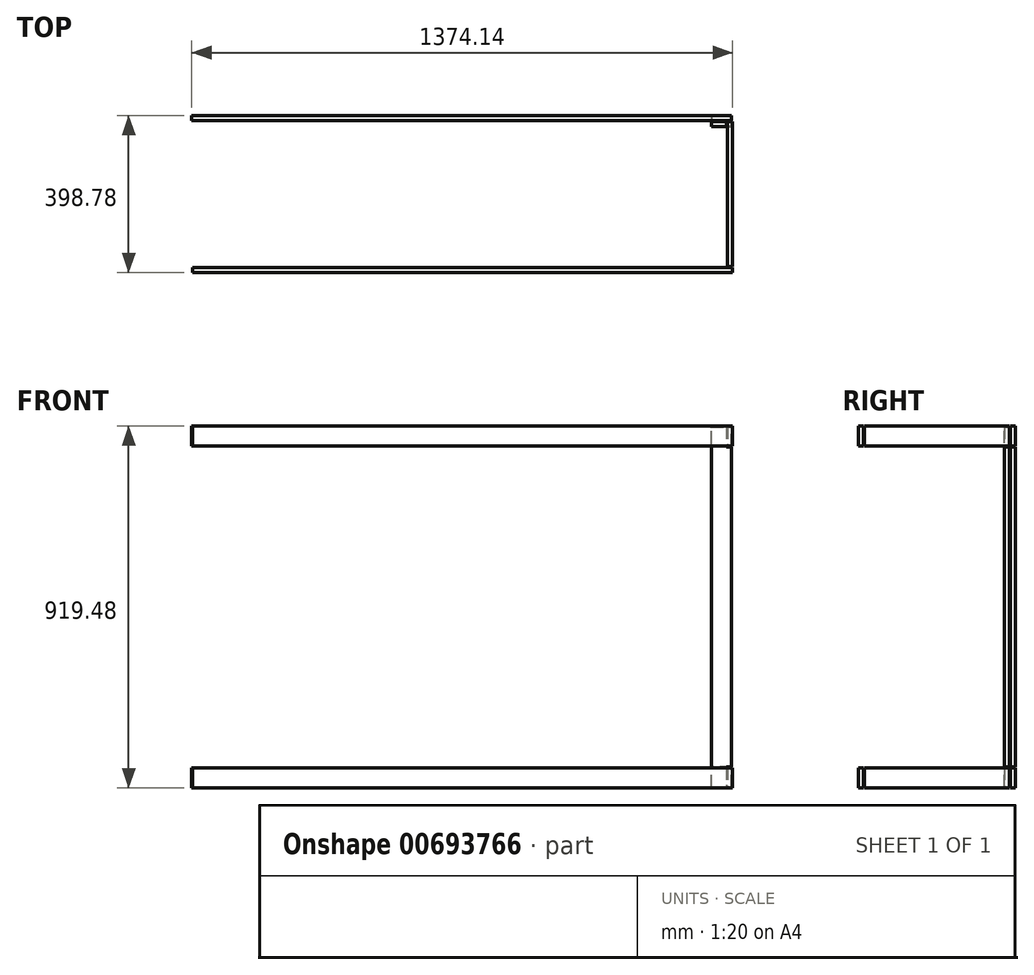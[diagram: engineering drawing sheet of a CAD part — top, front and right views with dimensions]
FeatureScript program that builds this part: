
annotation { "Feature Type Name" : "Feature", "Feature Type Description" : "" }
export const myFeature = defineFeature(function(context is Context, id is Id, definition is map)
    precondition{}
    {
        {
            var Q0;
            Q0=qCreatedBy(makeId("Front.planeOp"),FACE);
            var sketch = newSketch(context, id + "F0", { "sketchPlane" : qUnion([Q0])});
            skLineSegment(sketch, "E0.bottom", {"start": v(0, 0) * mm, "end": v(50.8, 0) * mm});
            skLineSegment(sketch, "E0.top", {"start": v(0, 914.4) * mm, "end": v(50.8, 914.4) * mm});
            skLineSegment(sketch, "E0.left", {"start": v(0, 0) * mm, "end": v(0, 914.4) * mm});
            skLineSegment(sketch, "E0.right", {"start": v(50.8, 0) * mm, "end": v(50.8, 914.4) * mm});
            skSolve(sketch);
        }
        {
            var Q0;
            Q0 = qSketchRegion(id + "F0", true);
            extrude(context, id + "F1", {"entities" : qUnion([Q0]), "depth" : 12.7 * mm, "offsetDistance" : 25.4 * mm});
        }
        {
            var Q0;
            Q0=makeQuery(id+"F1.opExtrude","CAP_FACE",FACE,{"disambiguationData":[OSD([sQuery(id+"F0.wireOp",EDGE,"E0.bottom"),sQuery(id+"F0.wireOp",EDGE,"E0.top"),sQuery(id+"F0.wireOp",EDGE,"E0.left"),sQuery(id+"F0.wireOp",EDGE,"E0.right")])],"isStart":true});
            cPlane(context, id + "F2", {"entities" : qUnion([Q0]), "cplaneType" : CPlaneType.OFFSET, "offset" : 2.54 * mm, "width" : 152.4 * mm, "height" : 152.4 * mm});
        }
        {
            var Q0;
            Q0=qCreatedBy(id+"F2.planeOp",FACE);
            var sketch = newSketch(context, id + "F3", { "sketchPlane" : qUnion([Q0])});
            skLineSegment(sketch, "E1.bottom", {"start": v(-50.8, 863.6) * mm, "end": v(0, 863.6) * mm});
            skLineSegment(sketch, "E1.top", {"start": v(-50.8, 50.8) * mm, "end": v(0, 50.8) * mm});
            skLineSegment(sketch, "E1.left", {"start": v(-50.8, 863.6) * mm, "end": v(-50.8, 50.8) * mm});
            skLineSegment(sketch, "E1.right", {"start": v(0, 863.6) * mm, "end": v(0, 50.8) * mm});
            skSolve(sketch);
        }
        {
            var Q0;
            Q0 = qSketchRegion(id + "F3", true);
            extrude(context, id + "F4", {"entities" : qUnion([Q0]), "depth" : 12.7 * mm, "offsetDistance" : 25.4 * mm});
        }
        {
            var Q0;
            Q0=makeQuery(id+"F4.opExtrude","SWEPT_FACE",FACE,{"disambiguationData":[OSD([sQuery(id+"F3.wireOp",EDGE,"E1.top")])]});
            cPlane(context, id + "F5", {"entities" : qUnion([Q0]), "cplaneType" : CPlaneType.OFFSET, "offset" : 2.54 * mm, "width" : 152.4 * mm, "height" : 152.4 * mm});
        }
        {
            var Q0;
            Q0=qCreatedBy(id+"F5.planeOp",FACE);
            var sketch = newSketch(context, id + "F6", { "sketchPlane" : qUnion([Q0])});
            skLineSegment(sketch, "E2.bottom", {"start": v(50.8, -2.54) * mm, "end": v(-1320.8, -2.54) * mm});
            skLineSegment(sketch, "E2.top", {"start": v(50.8, -15.24) * mm, "end": v(-1320.8, -15.24) * mm});
            skLineSegment(sketch, "E2.left", {"start": v(50.8, -2.54) * mm, "end": v(50.8, -15.24) * mm});
            skLineSegment(sketch, "E2.right", {"start": v(-1320.8, -2.54) * mm, "end": v(-1320.8, -15.24) * mm});
            skSolve(sketch);
        }
        {
            var Q0;
            Q0=makeQuery(id+"F6.imprint","IMPRINT",FACE,{"disambiguationData":[TD([[makeQuery(id+"F6.imprint","IMPRINT",EDGE,{"derivedFrom":sQuery(id+"F6.wireOp",EDGE,"E2.bottom")}),1.0]])]});
            extrude(context, id + "F7", {"entities" : qUnion([Q0]), "depth" : 50.8 * mm, "offsetDistance" : 25.4 * mm});
        }
        {
            var Q0;
            Q0=makeQuery(id+"F4.opExtrude","SWEPT_FACE",FACE,{"disambiguationData":[OSD([sQuery(id+"F3.wireOp",EDGE,"E1.bottom")])]});
            cPlane(context, id + "F8", {"entities" : qUnion([Q0]), "cplaneType" : CPlaneType.OFFSET, "offset" : 2.54 * mm, "width" : 152.4 * mm, "height" : 152.4 * mm});
        }
        {
            var Q0;
            Q0=qCreatedBy(id+"F8.planeOp",FACE);
            var sketch = newSketch(context, id + "F9", { "sketchPlane" : qUnion([Q0])});
            skLineSegment(sketch, "E3.bottom", {"start": v(50.8, 15.24) * mm, "end": v(-1320.8, 15.24) * mm});
            skLineSegment(sketch, "E3.top", {"start": v(50.8, 2.54) * mm, "end": v(-1320.8, 2.54) * mm});
            skLineSegment(sketch, "E3.left", {"start": v(50.8, 15.24) * mm, "end": v(50.8, 2.54) * mm});
            skLineSegment(sketch, "E3.right", {"start": v(-1320.8, 15.24) * mm, "end": v(-1320.8, 2.54) * mm});
            skSolve(sketch);
        }
        {
            var Q0;
            Q0=makeQuery(id+"F9.imprint","IMPRINT",FACE,{"disambiguationData":[TD([[makeQuery(id+"F9.imprint","IMPRINT",EDGE,{"derivedFrom":sQuery(id+"F9.wireOp",EDGE,"E3.bottom")}),1.0]])]});
            extrude(context, id + "F10", {"entities" : qUnion([Q0]), "depth" : 50.8 * mm, "offsetDistance" : 25.4 * mm});
        }
        {
            var Q0;
            Q0=makeQuery(id+"F1.opExtrude","CAP_FACE",FACE,{"disambiguationData":[OSD([sQuery(id+"F0.wireOp",EDGE,"E0.bottom"),sQuery(id+"F0.wireOp",EDGE,"E0.top"),sQuery(id+"F0.wireOp",EDGE,"E0.left"),sQuery(id+"F0.wireOp",EDGE,"E0.right")])],"isStart":false});
            var sketch = newSketch(context, id + "F11", { "sketchPlane" : qUnion([Q0])});
            skLineSegment(sketch, "E4.bottom", {"start": v(38.1, 914.4) * mm, "end": v(50.8, 914.4) * mm});
            skLineSegment(sketch, "E4.top", {"start": v(38.1, 863.6) * mm, "end": v(50.8, 863.6) * mm});
            skLineSegment(sketch, "E4.left", {"start": v(38.1, 914.4) * mm, "end": v(38.1, 863.6) * mm});
            skLineSegment(sketch, "E4.right", {"start": v(50.8, 914.4) * mm, "end": v(50.8, 863.6) * mm});
            skSolve(sketch);
        }
        {
            var Q0;
            Q0 = qSketchRegion(id + "F11", true);
            extrude(context, id + "F12", {"entities" : qUnion([Q0]), "operationType" : NewBodyOperationType.REMOVE, "oppositeDirection" : true, "depth" : 12.7 * mm, "offsetDistance" : 25.4 * mm});
        }
        {
            var Q0;
            Q0=makeQuery(id+"F12.boolean.opBoolean","COPY",FACE,{"derivedFrom":makeQuery(id+"F12.opExtrude","SWEPT_FACE",FACE,{"disambiguationData":[OSD([sQuery(id+"F11.wireOp",EDGE,"E4.left")])]})});
            cPlane(context, id + "F13", {"entities" : qUnion([Q0]), "cplaneType" : CPlaneType.OFFSET, "offset" : 2.54 * mm, "width" : 152.4 * mm, "height" : 152.4 * mm});
        }
        {
            var Q0;
            Q0=qCreatedBy(id+"F13.planeOp",FACE);
            var sketch = newSketch(context, id + "F14", { "sketchPlane" : qUnion([Q0])});
            skLineSegment(sketch, "E5.bottom", {"start": v(-368.3, 916.94) * mm, "end": v(0, 916.94) * mm});
            skLineSegment(sketch, "E5.top", {"start": v(-368.3, 866.14) * mm, "end": v(0, 866.14) * mm});
            skLineSegment(sketch, "E5.left", {"start": v(-368.3, 916.94) * mm, "end": v(-368.3, 866.14) * mm});
            skLineSegment(sketch, "E5.right", {"start": v(0, 916.94) * mm, "end": v(0, 866.14) * mm});
            skSolve(sketch);
        }
        {
            var Q0;
            Q0=makeQuery(id+"F14.imprint","IMPRINT",FACE,{"disambiguationData":[TD([[makeQuery(id+"F14.imprint","IMPRINT",EDGE,{"derivedFrom":sQuery(id+"F14.wireOp",EDGE,"E5.bottom")}),-1.0]])]});
            extrude(context, id + "F15", {"entities" : qUnion([Q0]), "depth" : 12.7 * mm, "offsetDistance" : 25.4 * mm});
        }
        {
            var Q0;
            Q0=makeQuery(id+"F1.opExtrude","CAP_FACE",FACE,{"disambiguationData":[OSD([sQuery(id+"F0.wireOp",EDGE,"E0.bottom"),sQuery(id+"F0.wireOp",EDGE,"E0.top"),sQuery(id+"F0.wireOp",EDGE,"E0.left"),sQuery(id+"F0.wireOp",EDGE,"E0.right")])],"isStart":false});
            var sketch = newSketch(context, id + "F16", { "sketchPlane" : qUnion([Q0])});
            skLineSegment(sketch, "E6.bottom", {"start": v(50.8, 50.8) * mm, "end": v(38.1, 50.8) * mm});
            skLineSegment(sketch, "E6.top", {"start": v(50.8, 0) * mm, "end": v(38.1, 0) * mm});
            skLineSegment(sketch, "E6.left", {"start": v(50.8, 50.8) * mm, "end": v(50.8, 0) * mm});
            skLineSegment(sketch, "E6.right", {"start": v(38.1, 50.8) * mm, "end": v(38.1, 0) * mm});
            skSolve(sketch);
        }
        {
            var Q0;
            Q0 = qSketchRegion(id + "F16", true);
            extrude(context, id + "F17", {"entities" : qUnion([Q0]), "operationType" : NewBodyOperationType.REMOVE, "oppositeDirection" : true, "depth" : 12.7 * mm, "offsetDistance" : 25.4 * mm});
        }
        {
            var Q0;
            Q0=makeQuery(id+"F17.boolean.opBoolean","COPY",FACE,{"derivedFrom":makeQuery(id+"F17.opExtrude","SWEPT_FACE",FACE,{"disambiguationData":[OSD([sQuery(id+"F16.wireOp",EDGE,"E6.right")])]})});
            cPlane(context, id + "F18", {"entities" : qUnion([Q0]), "cplaneType" : CPlaneType.OFFSET, "offset" : 2.54 * mm, "width" : 152.4 * mm, "height" : 152.4 * mm});
        }
        {
            var Q0;
            Q0=qCreatedBy(id+"F18.planeOp",FACE);
            var sketch = newSketch(context, id + "F19", { "sketchPlane" : qUnion([Q0])});
            skLineSegment(sketch, "E7.bottom", {"start": v(0, 48.26) * mm, "end": v(-368.3, 48.26) * mm});
            skLineSegment(sketch, "E7.top", {"start": v(0, -2.54) * mm, "end": v(-368.3, -2.54) * mm});
            skLineSegment(sketch, "E7.left", {"start": v(0, 48.26) * mm, "end": v(0, -2.54) * mm});
            skLineSegment(sketch, "E7.right", {"start": v(-368.3, 48.26) * mm, "end": v(-368.3, -2.54) * mm});
            skSolve(sketch);
        }
        {
            var Q0;
            Q0=makeQuery(id+"F19.imprint","IMPRINT",FACE,{"disambiguationData":[TD([[makeQuery(id+"F19.imprint","IMPRINT",EDGE,{"derivedFrom":sQuery(id+"F19.wireOp",EDGE,"E7.bottom")}),1.0]])]});
            extrude(context, id + "F20", {"entities" : qUnion([Q0]), "depth" : 12.7 * mm, "offsetDistance" : 25.4 * mm});
        }
        {
            var Q0;
            Q0=makeQuery(id+"F15.opExtrude","SWEPT_FACE",FACE,{"disambiguationData":[OSD([sQuery(id+"F14.wireOp",EDGE,"E5.left")])]});
            cPlane(context, id + "F21", {"entities" : qUnion([Q0]), "cplaneType" : CPlaneType.OFFSET, "offset" : 2.54 * mm, "width" : 152.4 * mm, "height" : 152.4 * mm});
        }
        {
            var Q0;
            Q0=qCreatedBy(id+"F21.planeOp",FACE);
            var sketch = newSketch(context, id + "F22", { "sketchPlane" : qUnion([Q0])});
            skLineSegment(sketch, "E8.bottom", {"start": v(53.34, 916.94) * mm, "end": v(-1318.26, 916.94) * mm});
            skLineSegment(sketch, "E8.top", {"start": v(53.34, 866.14) * mm, "end": v(-1318.26, 866.14) * mm});
            skLineSegment(sketch, "E8.left", {"start": v(53.34, 916.94) * mm, "end": v(53.34, 866.14) * mm});
            skLineSegment(sketch, "E8.right", {"start": v(-1318.26, 916.94) * mm, "end": v(-1318.26, 866.14) * mm});
            skSolve(sketch);
        }
        {
            var Q0;
            Q0=makeQuery(id+"F22.imprint","IMPRINT",FACE,{"disambiguationData":[TD([[makeQuery(id+"F22.imprint","IMPRINT",EDGE,{"derivedFrom":sQuery(id+"F22.wireOp",EDGE,"E8.bottom")}),1.0]])]});
            extrude(context, id + "F23", {"entities" : qUnion([Q0]), "depth" : 12.7 * mm, "offsetDistance" : 25.4 * mm});
        }
        {
            var Q0;
            Q0=makeQuery(id+"F20.opExtrude","SWEPT_FACE",FACE,{"disambiguationData":[OSD([sQuery(id+"F19.wireOp",EDGE,"E7.right")])]});
            cPlane(context, id + "F24", {"entities" : qUnion([Q0]), "cplaneType" : CPlaneType.OFFSET, "offset" : 2.54 * mm, "width" : 152.4 * mm, "height" : 152.4 * mm});
        }
        {
            var Q0;
            Q0=qCreatedBy(id+"F24.planeOp",FACE);
            var sketch = newSketch(context, id + "F25", { "sketchPlane" : qUnion([Q0])});
            skLineSegment(sketch, "E9.bottom", {"start": v(-1318.26, 48.26) * mm, "end": v(53.34, 48.26) * mm});
            skLineSegment(sketch, "E9.top", {"start": v(-1318.26, -2.54) * mm, "end": v(53.34, -2.54) * mm});
            skLineSegment(sketch, "E9.left", {"start": v(-1318.26, 48.26) * mm, "end": v(-1318.26, -2.54) * mm});
            skLineSegment(sketch, "E9.right", {"start": v(53.34, 48.26) * mm, "end": v(53.34, -2.54) * mm});
            skSolve(sketch);
        }
        {
            var Q0;
            Q0=makeQuery(id+"F25.imprint","IMPRINT",FACE,{"disambiguationData":[TD([[makeQuery(id+"F25.imprint","IMPRINT",EDGE,{"derivedFrom":sQuery(id+"F25.wireOp",EDGE,"E9.bottom")}),-1.0]])]});
            extrude(context, id + "F26", {"entities" : qUnion([Q0]), "depth" : 12.7 * mm, "offsetDistance" : 25.4 * mm});
        }
    });
